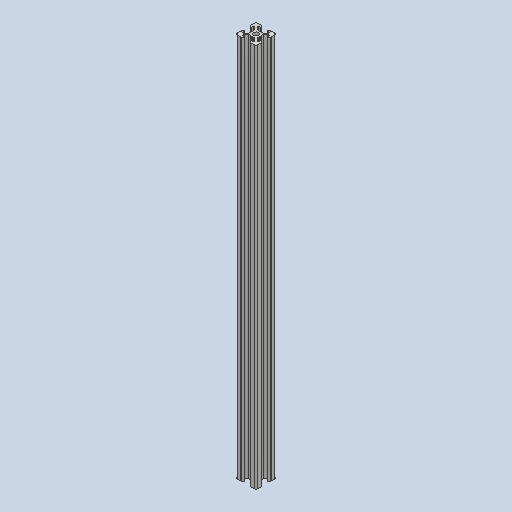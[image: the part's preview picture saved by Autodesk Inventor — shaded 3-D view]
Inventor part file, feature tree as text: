
AUTODESK INVENTOR PART (.ipt)
format: ipt  version: 2025.2 (Build 292293000, 293)  size: 251,392 bytes
history: native  units: mm
features: other x1, extrude x1, sketch x1
ambient origin geometry x8: Origin, YZ Plane, XZ Plane, XY Plane, X Axis, Y Axis, Z Axis, Center Point
bodies: Body1 (feature_tree)
feature tree (3):
  other  "Твердое тело1"
  extrude  "Выдавливание1"  Depth=0.25mm
  sketch  "Эскиз1"
